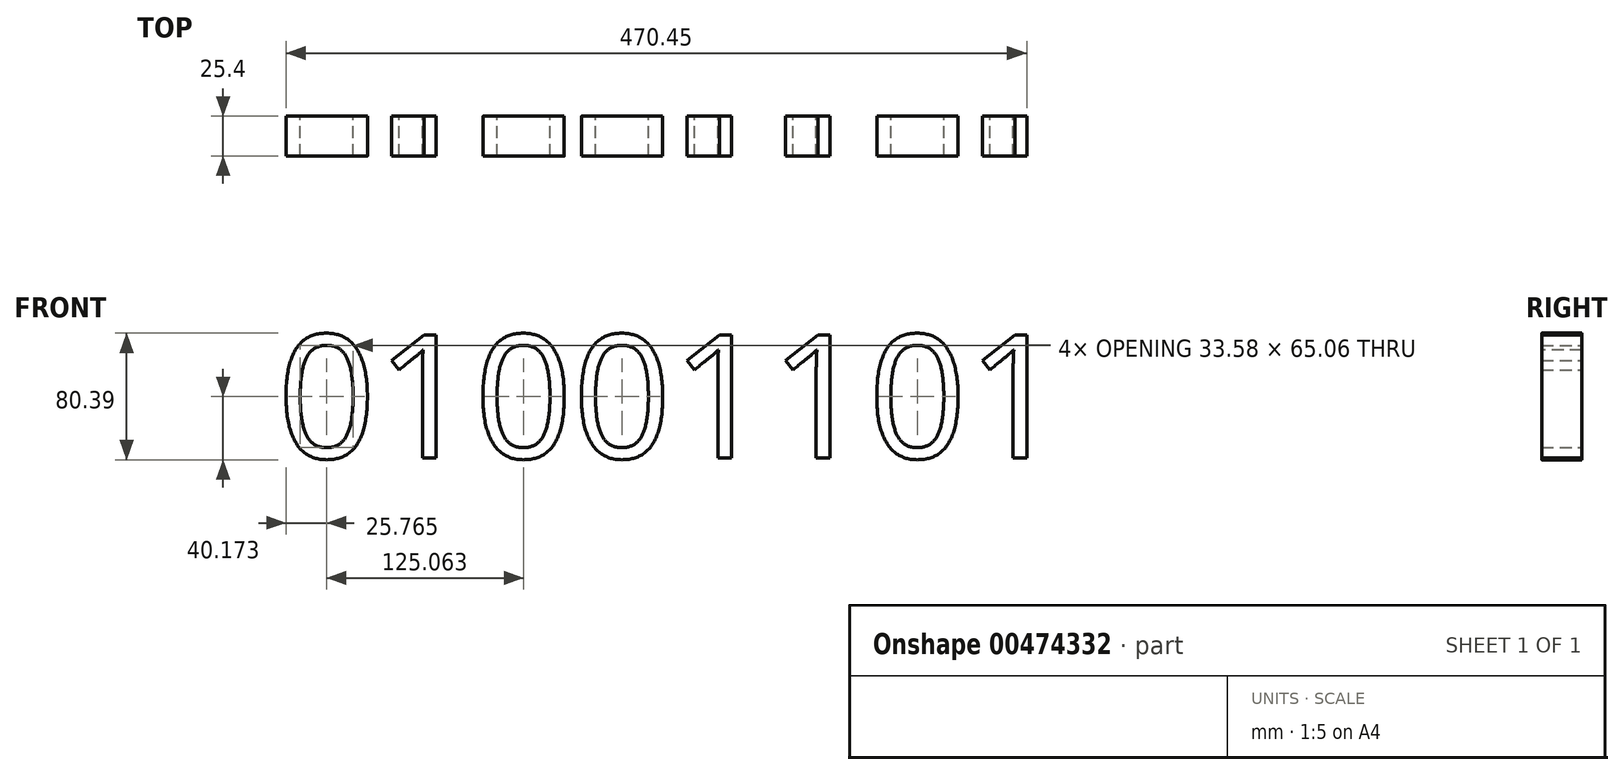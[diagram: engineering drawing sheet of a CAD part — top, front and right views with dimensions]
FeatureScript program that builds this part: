
annotation { "Feature Type Name" : "Feature", "Feature Type Description" : "" }
export const myFeature = defineFeature(function(context is Context, id is Id, definition is map)
    precondition{}
    {
        {
            var Q0;
            Q0=qCreatedBy(makeId("Front.planeOp"),FACE);
            var sketch = newSketch(context, id + "F0", { "sketchPlane" : qUnion([Q0])});
            skText(sketch, "E0", { "text": "01001101", "fontName": "OpenSans-Regular.ttf"});
            const initialGuessF0  = {"E0": [-0.033, -0.03417, 1, 0, 0.07875]};
            skSetInitialGuess(sketch, initialGuessF0);
            skSolve(sketch);
        }
        {
            var Q0;
            Q0=qSketchRegion(id+"F0",true);
            extrude(context, id + "F1", {"entities" : qUnion([Q0]), "depth" : 25.4 * mm});
        }
    });
